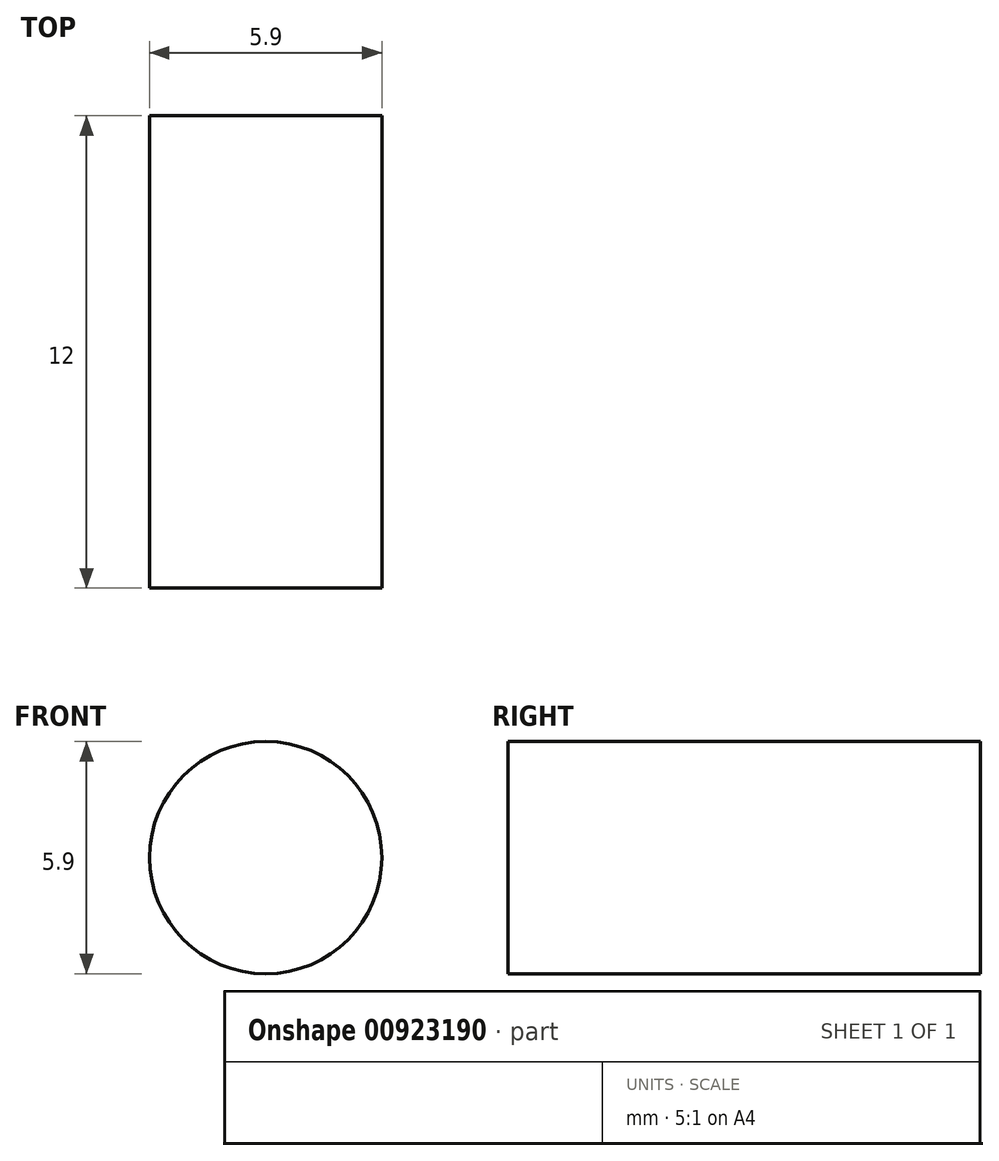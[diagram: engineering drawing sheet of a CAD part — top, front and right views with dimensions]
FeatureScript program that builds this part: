
annotation { "Feature Type Name" : "Feature", "Feature Type Description" : "" }
export const myFeature = defineFeature(function(context is Context, id is Id, definition is map)
    precondition{}
    {
        {
            var Q0;
            Q0=qCreatedBy(makeId("Front.planeOp"),FACE);
            var sketch = newSketch(context, id + "F0", { "sketchPlane" : qUnion([Q0])});
            skCircle(sketch, "E0", {"center": v(0, 0) * mm, "radius": 2.95 * mm});
            skSolve(sketch);
        }
        {
            var Q0;
            Q0=makeQuery(id+"F0.imprint","IMPRINT",FACE,{"disambiguationData":[TD([[makeQuery(id+"F0.imprint","IMPRINT",EDGE,{"derivedFrom":sQuery(id+"F0.wireOp",EDGE,"E0")}),1.0]])]});
            extrude(context, id + "F1", {"entities" : qUnion([Q0]), "depth" : 12 * mm, "offsetDistance" : 25 * mm});
        }
    });
